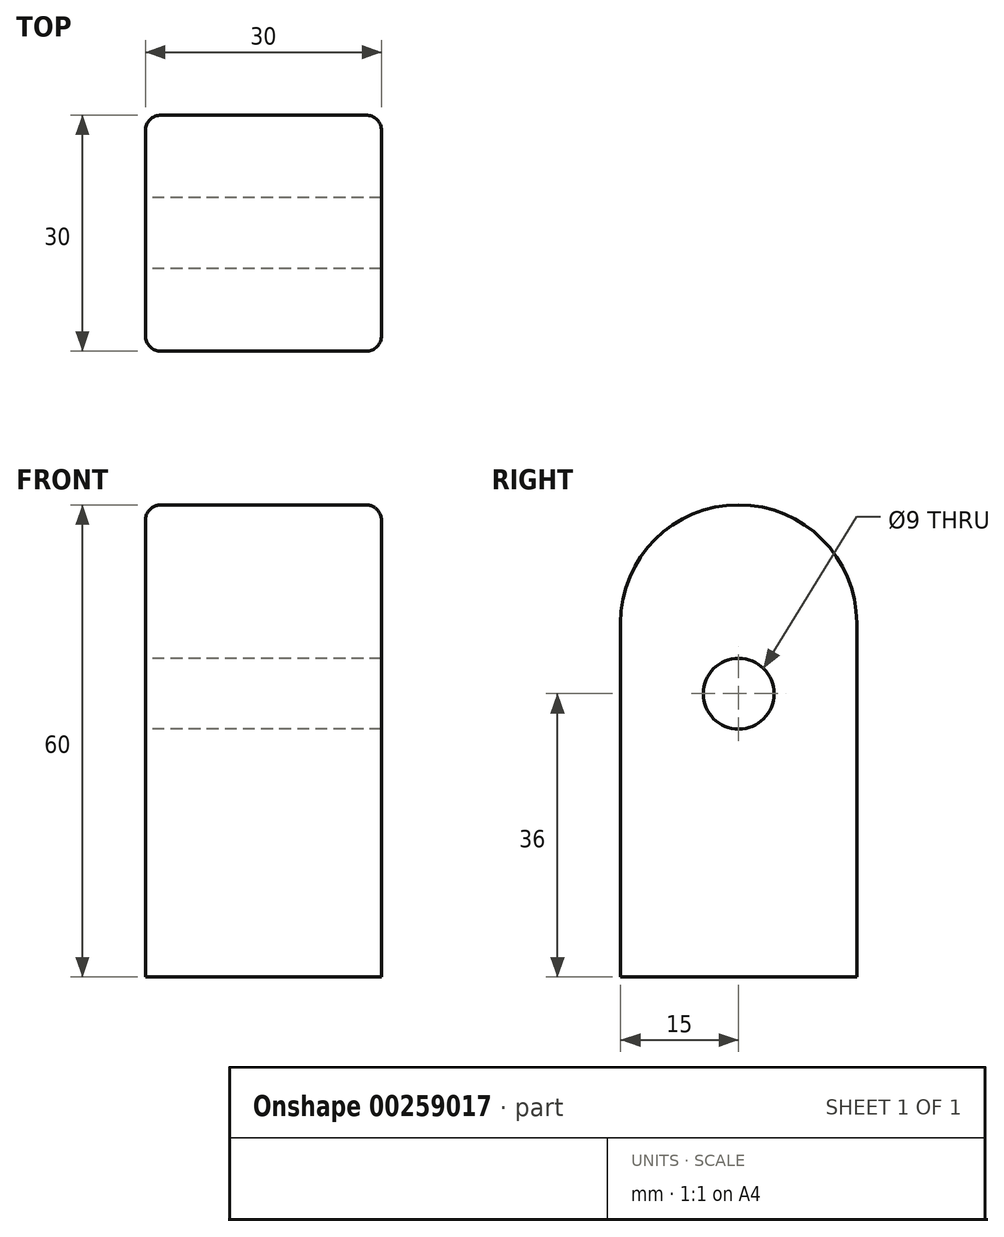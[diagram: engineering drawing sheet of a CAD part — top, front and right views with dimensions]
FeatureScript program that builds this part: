
annotation { "Feature Type Name" : "Feature", "Feature Type Description" : "" }
export const myFeature = defineFeature(function(context is Context, id is Id, definition is map)
    precondition{}
    {
        {
            var Q0;
            Q0=qCreatedBy(makeId("Right.planeOp"),FACE);
            var sketch = newSketch(context, id + "F0", { "sketchPlane" : qUnion([Q0])});
            skLineSegment(sketch, "E0.bottom", {"start": v(15, 30) * mm, "end": v(-15, 30) * mm});
            skLineSegment(sketch, "E0.top", {"start": v(15, -30) * mm, "end": v(-15, -30) * mm});
            skLineSegment(sketch, "E0.left", {"start": v(15, 30) * mm, "end": v(15, -30) * mm});
            skLineSegment(sketch, "E0.right", {"start": v(-15, 30) * mm, "end": v(-15, -30) * mm});
            skPoint(sketch, "E0.middle", {"position": v(0, 0) * mm});
            skSolve(sketch);
        }
        {
            var Q0;
            Q0=makeQuery(id+"F0.imprint","IMPRINT",FACE,{"disambiguationData":[TD([[makeQuery(id+"F0.imprint","IMPRINT",EDGE,{"derivedFrom":sQuery(id+"F0.wireOp",EDGE,"E0.bottom")}),1.0]])]});
            extrude(context, id + "F1", {"entities" : qUnion([Q0]), "depth" : 30 * mm, "offsetDistance" : 25 * mm, "symmetric" : true});
        }
        {
            var Q0;
            Q0=makeQuery(id+"F1.opExtrude","CAP_FACE",FACE,{"disambiguationData":[OSD([sQuery(id+"F0.wireOp",EDGE,"E0.bottom"),sQuery(id+"F0.wireOp",EDGE,"E0.top"),sQuery(id+"F0.wireOp",EDGE,"E0.left"),sQuery(id+"F0.wireOp",EDGE,"E0.right")])],"isStart":false});
            var sketch = newSketch(context, id + "F2", { "sketchPlane" : qUnion([Q0])});
            skLineSegment(sketch, "E1", {"start": v(0, 30) * mm, "end": v(0, -30) * mm, "construction": true});
            skPoint(sketch, "E2", {"position": v(0, 6) * mm});
            skSolve(sketch);
        }
        {
            var Q0;
            Q0=makeQuery(id+"F1.opExtrude","SWEPT_EDGE",EDGE,{"disambiguationData":[OSD([sQuery(id+"F0.wireOp",EDGE,"E0.bottom"),sQuery(id+"F0.wireOp",EDGE,"E0.right")])]});
            var Q1;
            Q1=makeQuery(id+"F1.opExtrude","SWEPT_EDGE",EDGE,{"disambiguationData":[OSD([sQuery(id+"F0.wireOp",EDGE,"E0.bottom"),sQuery(id+"F0.wireOp",EDGE,"E0.left")])]});
            fillet(context, id + "F3", {"entities" : qUnion([Q0, Q1]), "radius" : 15 * mm, "tangentPropagation" : true, "allowEdgeOverflow" : false});
        }
        {
            var Q0;
            Q0=makeQuery(id+"F1.opExtrude","CAP_EDGE",EDGE,{"disambiguationData":[OSD([sQuery(id+"F0.wireOp",EDGE,"E0.right")])],"isStart":false});
            var Q1;
            Q1=makeQuery(id+"F1.opExtrude","CAP_EDGE",EDGE,{"disambiguationData":[OSD([sQuery(id+"F0.wireOp",EDGE,"E0.left")])],"isStart":true});
            var Q2;
            {var subQ0=sQuery(id+"F0.wireOp",EDGE,"E0.right");var subQ1=sQuery(id+"F0.wireOp",EDGE,"E0.bottom");Q2=makeQuery(id+"F3.opFillet","BLEND_EDGE",EDGE,{"blendedFrom":[makeQuery(id+"F1.opExtrude","SWEPT_EDGE",EDGE,{"disambiguationData":[OSD([subQ1,subQ0])]}),makeQuery(id+"F1.opExtrude","CAP_FACE",FACE,{"disambiguationData":[OSD([subQ1,sQuery(id+"F0.wireOp",EDGE,"E0.top"),sQuery(id+"F0.wireOp",EDGE,"E0.left"),subQ0])],"isStart":true})],"blendedInto":[makeQuery(id+"F1.opExtrude","CAP_FACE",FACE,{"disambiguationData":[OSD([subQ1,sQuery(id+"F0.wireOp",EDGE,"E0.top"),sQuery(id+"F0.wireOp",EDGE,"E0.left"),subQ0])],"isStart":true})]});}
            fillet(context, id + "F4", {"entities" : qUnion([Q0, Q1, Q2]), "radius" : 2 * mm, "tangentPropagation" : true, "allowEdgeOverflow" : false});
        }
        {
            var Q0;
            Q0=sQuery(id+"F2.wireOp",VERTEX,"E2");
            var Q1;
            Q1=makeQuery(id+"F1.opExtrude","SWEPT_BODY",BODY,{"disambiguationData":[OSD([sQuery(id+"F0.wireOp",EDGE,"E0.bottom"),sQuery(id+"F0.wireOp",EDGE,"E0.top"),sQuery(id+"F0.wireOp",EDGE,"E0.left"),sQuery(id+"F0.wireOp",EDGE,"E0.right")])]});
            hole(context, id + "F5", {"style" : HoleStyle.SIMPLE, "endStyle" : HoleEndStyle.THROUGH, "holeDiameter" : 9 * mm, "majorDiameter" : 5 * mm, "isTappedThrough" : true, "tappedDepth" : 12 * mm, "tapClearance" : 3, "startFromSketch" : true, "locations" : qUnion([Q0]), "scope" : qUnion([Q1])});
        }
    });
